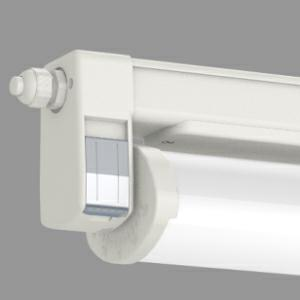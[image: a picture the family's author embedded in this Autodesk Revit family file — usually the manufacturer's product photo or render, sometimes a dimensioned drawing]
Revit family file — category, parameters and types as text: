
# Revit family: bitburg_led_m1500_-_7830lm__pc_tropal_r___bruchsicher____840_4000k__raumstrahlend_6456803484-e-mc9_7fd5
name_source: partatom
category: Lighting Fixtures
units: mm (PartAtom-declared; Revit-internal decimal feet)

## family parameters
Cut with Voids When Loaded = No
Host = Face
Light Source = No
Part Type = Normal
Room Calculation Point = No
Round Connector Dimension = Use Diameter
Shared = No

## types (1)
- BITBURG LED m1500 - 7830lm, PC Tropal® (bruchsicher) , 840/4000K, raumstrahlend (1 x LED Stripe, 7830 lm, 41 W, 840/4000K)
    Apparent Load = 44 VA
    Approval mark = CE, ENEC
    CIE Flux Codes = 56 85 96 98 98
    Color Rendering = 1B/80..89
    Color Temperature = 840/4000K
    Default Elevation = 1800 mm
    Description = Polymer luminaire for surface ceiling and wall surface-mounting for HACCP/IFS applications with LED lamps. Useable in production facilities and suppliers in the food and beverage industry. Acid, alkaline and fuel-resistant luminaire housing made of fibreglass reinforced polymer, similar to RAL 9010. Useable for indoor and outdoor areas according to protection rating IP 65, IP 66 and IP 67. Suitable for intensive cleaning processes using pressure washers due to high protection rating IP 69K. Thermally separated lamp chamber and driver chamber. Short sealing system consisting of age-resistant, form-retaining silicone/synthetic rubber. Profile including coating for increased resistance against acids, bases, and cleaning agents. Reflector tube that can be swivelled made of PMMA Transopal® (impact strengthened) or PC Tropal® (fracture proof) with internal aluminium reflector (MIRO-SILVER®). Reflector tube can be locked in increments of 10°. Luminaire ready for mounting and installation. Built-in driver 230 V AC/DC. Two access covers, two cable glands on face side M20 and 4 x 1.5 mm² through wiring. 2 kV transient filter. Single or row mounting. Ceiling installation using two stainless steel mounting clamps, variable mounting distance. Captive end caps.


Length: 1551 mm
Width: 107 mm
Height: 140 mm
Weight: 4.2 kg

LOR: 97.7 %
    Height = 140 mm  [stored 0.459318 ft]
    Lamp = 1 x LED Stripe
    Lamp Light Flux = 7830 lm
    Lamp Power = 41 W
    Lamp count = 1
    Length = 1551 mm
    Lifetime = 60000 h
    Luminous efficacy = 174 lm/W
    Manufacturer = NORKA
    ModVariant = No
    Model = 6456803484-E-MC9
    Mounting Place = Ceiling, Wall
    Mounting Type = Rail mounted, Pendant
    Number of Poles = 1
    OnlyDefault = Yes
    Power Factor = 1
    Product Name = BITBURG LED m1500 - 7830lm, PC Tropal® (bruchsicher) , 840/4000K, raumstrahlend
    Product group = Ceiling-/wall luminaire
    ProductGroupID = 30
    Protection Class = Protection class II
    Protection Degree = IP 65
    RLX_Detail_Level = 1
    RlxData = <blob elided: 222693 chars, md5=bf0c992e>
    Socket = socket
    Standby Power = 0 W
    System Light Flux = 7650 lm
    System Power = 44 W
    Type Comments = Product without accessories
    Type Image = bitburg-led-transopal.jpg
    URL = http://relux.com
    VarID = ---
    Voltage = 0 V
    Weight = 0.00 kg
    Width = 107 mm

note: [stored X ft] marks values corroborated as IEEE doubles in the binary element streams (Revit-internal decimal feet)

## geometry (parser evidence)
native form markers: Blend x4, Sweep x14
no freeform markers — native parametric forms only
